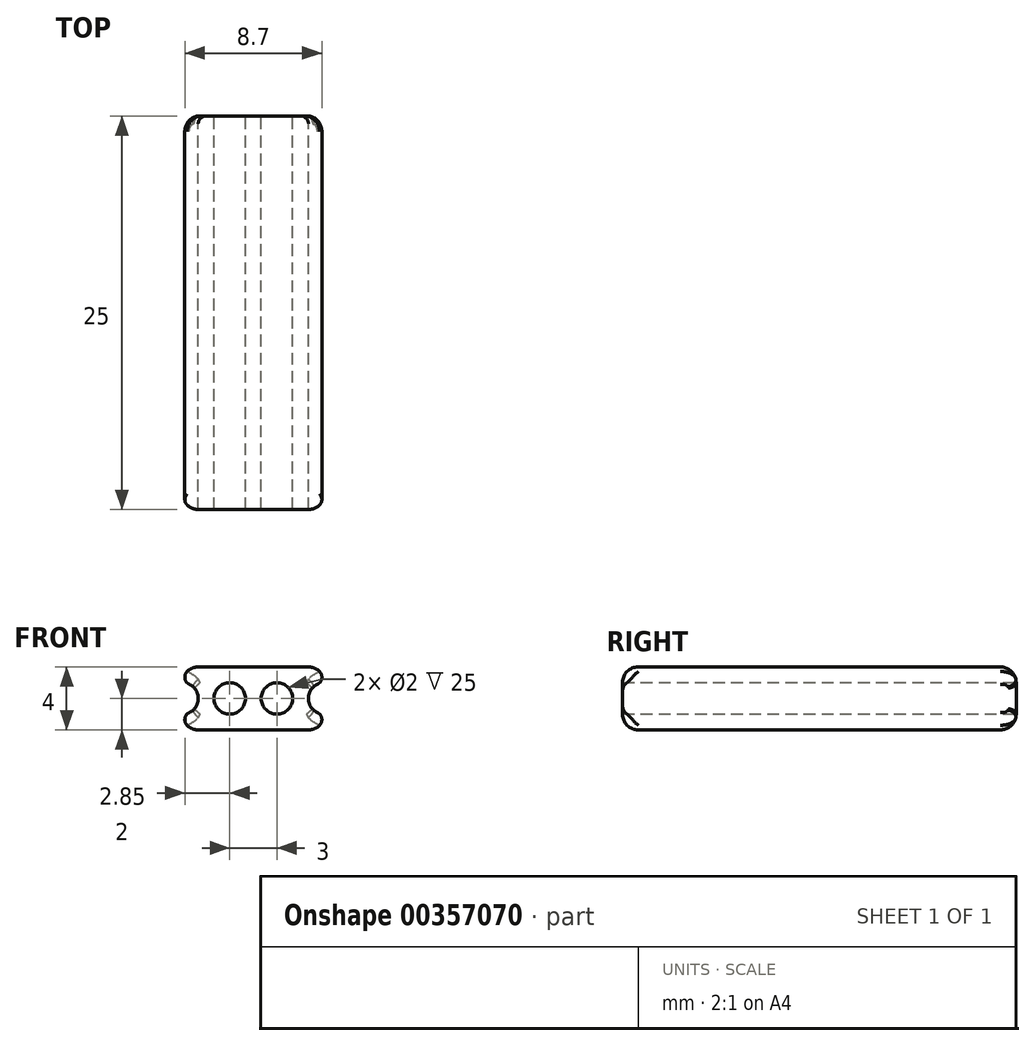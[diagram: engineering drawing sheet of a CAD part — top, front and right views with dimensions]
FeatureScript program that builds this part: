
annotation { "Feature Type Name" : "Feature", "Feature Type Description" : "" }
export const myFeature = defineFeature(function(context is Context, id is Id, definition is map)
    precondition{}
    {
        {
            var Q0;
            Q0=qCreatedBy(makeId("Front.planeOp"),FACE);
            var sketch = newSketch(context, id + "F0", { "sketchPlane" : qUnion([Q0])});
            skLineSegment(sketch, "E0.bottom", {"start": v(-4.5, 2) * mm, "end": v(4.5, 2) * mm});
            skLineSegment(sketch, "E0.top", {"start": v(-4.5, -2) * mm, "end": v(4.5, -2) * mm});
            skLineSegment(sketch, "E0.left", {"start": v(-4.5, 2) * mm, "end": v(-4.5, -2) * mm});
            skLineSegment(sketch, "E0.right", {"start": v(4.5, 2) * mm, "end": v(4.5, -2) * mm});
            skPoint(sketch, "E1", {"position": v(0, 2) * mm});
            skPoint(sketch, "E2", {"position": v(-4.5, 0) * mm});
            skCircle(sketch, "E3", {"center": v(-4.5, 0) * mm, "radius": 1 * mm});
            skCircle(sketch, "E4.1.0.0", {"center": v(-1.5, 0) * mm, "radius": 1 * mm});
            skCircle(sketch, "E4.2.0.0", {"center": v(1.5, 0) * mm, "radius": 1 * mm});
            skCircle(sketch, "E4.3.0.0", {"center": v(4.5, 0) * mm, "radius": 1 * mm});
            skLineSegment(sketch, "E4.direction1", {"start": v(-4.5, 0) * mm, "end": v(-1.5, 0) * mm, "construction": true});
            skSolve(sketch);
        }
        {
            var Q0;
            Q0=makeQuery(id+"F0.imprint","IMPRINT",FACE,{"disambiguationData":[TD([[makeQuery(id+"F0.imprint","IMPRINT",EDGE,{"derivedFrom":sQuery(id+"F0.wireOp",EDGE,"E0.bottom")}),-1.0]])]});
            extrude(context, id + "F1", {"entities" : qUnion([Q0]), "endBound" : BoundingType.SYMMETRIC, "depth" : 25 * mm, "offsetDistance" : 25 * mm});
        }
        {
            var Q0;
            Q0=makeQuery(id+"F1.opExtrude","SWEPT_FACE",FACE,{"disambiguationData":[OSD([sQuery(id+"F0.wireOp",EDGE,"E0.bottom")])]});
            var Q1;
            Q1=makeQuery(id+"F1.opExtrude","SWEPT_FACE",FACE,{"disambiguationData":[OSD([sQuery(id+"F0.wireOp",EDGE,"E0.top")])]});
            var Q2;
            {var subQ0=sQuery(id+"F0.wireOp",EDGE,"E0.right");Q2=makeQuery(id+"F1.opExtrude","CAP_EDGE",EDGE,{"disambiguationData":[OSD([subQ0]),TDD([makeQuery(id+"F0.imprint","IMPRINT",EDGE,{"disambiguationData":[TD([[makeQuery(id+"F0.imprint","INTERSECT",VERTEX,{"derivedFrom":[sQuery(id+"F0.wireOp",EDGE,"E0.bottom"),subQ0]}),-1.0]])],"derivedFrom":subQ0})])],"isStart":false});}
            var Q3;
            {var subQ0=sQuery(id+"F0.wireOp",EDGE,"E0.right");Q3=makeQuery(id+"F1.opExtrude","CAP_EDGE",EDGE,{"disambiguationData":[OSD([subQ0]),TDD([makeQuery(id+"F0.imprint","IMPRINT",EDGE,{"disambiguationData":[TD([[makeQuery(id+"F0.imprint","INTERSECT",VERTEX,{"derivedFrom":[sQuery(id+"F0.wireOp",EDGE,"E0.top"),subQ0]}),1.0]])],"derivedFrom":subQ0})])],"isStart":false});}
            var Q4;
            {var subQ0=sQuery(id+"F0.wireOp",EDGE,"E0.left");Q4=makeQuery(id+"F1.opExtrude","CAP_EDGE",EDGE,{"disambiguationData":[OSD([subQ0]),TDD([makeQuery(id+"F0.imprint","IMPRINT",EDGE,{"disambiguationData":[TD([[makeQuery(id+"F0.imprint","INTERSECT",VERTEX,{"derivedFrom":[sQuery(id+"F0.wireOp",EDGE,"E0.bottom"),subQ0]}),-1.0]])],"derivedFrom":subQ0})])],"isStart":false});}
            var Q5;
            {var subQ0=sQuery(id+"F0.wireOp",EDGE,"E0.left");Q5=makeQuery(id+"F1.opExtrude","CAP_EDGE",EDGE,{"disambiguationData":[OSD([subQ0]),TDD([makeQuery(id+"F0.imprint","IMPRINT",EDGE,{"disambiguationData":[TD([[makeQuery(id+"F0.imprint","INTERSECT",VERTEX,{"derivedFrom":[sQuery(id+"F0.wireOp",EDGE,"E0.top"),subQ0]}),1.0]])],"derivedFrom":subQ0})])],"isStart":false});}
            var Q6;
            {var subQ0=sQuery(id+"F0.wireOp",EDGE,"E0.left");Q6=makeQuery(id+"F1.opExtrude","CAP_EDGE",EDGE,{"disambiguationData":[OSD([subQ0]),TDD([makeQuery(id+"F0.imprint","IMPRINT",EDGE,{"disambiguationData":[TD([[makeQuery(id+"F0.imprint","INTERSECT",VERTEX,{"derivedFrom":[sQuery(id+"F0.wireOp",EDGE,"E0.bottom"),subQ0]}),-1.0]])],"derivedFrom":subQ0})])],"isStart":true});}
            var Q7;
            {var subQ0=sQuery(id+"F0.wireOp",EDGE,"E0.left");Q7=makeQuery(id+"F1.opExtrude","CAP_EDGE",EDGE,{"disambiguationData":[OSD([subQ0]),TDD([makeQuery(id+"F0.imprint","IMPRINT",EDGE,{"disambiguationData":[TD([[makeQuery(id+"F0.imprint","INTERSECT",VERTEX,{"derivedFrom":[sQuery(id+"F0.wireOp",EDGE,"E0.top"),subQ0]}),1.0]])],"derivedFrom":subQ0})])],"isStart":true});}
            var Q8;
            {var subQ0=sQuery(id+"F0.wireOp",EDGE,"E0.right");Q8=makeQuery(id+"F1.opExtrude","CAP_EDGE",EDGE,{"disambiguationData":[OSD([subQ0]),TDD([makeQuery(id+"F0.imprint","IMPRINT",EDGE,{"disambiguationData":[TD([[makeQuery(id+"F0.imprint","INTERSECT",VERTEX,{"derivedFrom":[sQuery(id+"F0.wireOp",EDGE,"E0.bottom"),subQ0]}),-1.0]])],"derivedFrom":subQ0})])],"isStart":true});}
            var Q9;
            {var subQ0=sQuery(id+"F0.wireOp",EDGE,"E0.right");Q9=makeQuery(id+"F1.opExtrude","CAP_EDGE",EDGE,{"disambiguationData":[OSD([subQ0]),TDD([makeQuery(id+"F0.imprint","IMPRINT",EDGE,{"disambiguationData":[TD([[makeQuery(id+"F0.imprint","INTERSECT",VERTEX,{"derivedFrom":[sQuery(id+"F0.wireOp",EDGE,"E0.top"),subQ0]}),1.0]])],"derivedFrom":subQ0})])],"isStart":true});}
            fillet(context, id + "F2", {"entities" : qUnion([Q0, Q1, Q2, Q3, Q4, Q5, Q6, Q7, Q8, Q9]), "radius" : 1 * mm, "tangentPropagation" : true, "allowEdgeOverflow" : false});
        }
        {
            var Q0;
            {var subQ0=sQuery(id+"F0.wireOp",EDGE,"E3");var subQ1=sQuery(id+"F0.wireOp",EDGE,"E0.left");Q0=makeQuery(id+"F2.opFillet","BLEND_EDGE",EDGE,{"blendedFrom":[makeQuery(id+"F1.opExtrude","CAP_EDGE",EDGE,{"disambiguationData":[OSD([subQ1]),TDD([makeQuery(id+"F0.imprint","IMPRINT",EDGE,{"disambiguationData":[TD([[makeQuery(id+"F0.imprint","INTERSECT",VERTEX,{"derivedFrom":[sQuery(id+"F0.wireOp",EDGE,"E0.bottom"),subQ1]}),-1.0]])],"derivedFrom":subQ1})])],"isStart":true}),makeQuery(id+"F1.opExtrude","SWEPT_FACE",FACE,{"disambiguationData":[OSD([subQ0])]})],"blendedInto":[makeQuery(id+"F1.opExtrude","SWEPT_FACE",FACE,{"disambiguationData":[OSD([subQ0])]})]});}
            var Q1;
            {var subQ0=sQuery(id+"F0.wireOp",EDGE,"E3");var subQ1=sQuery(id+"F0.wireOp",EDGE,"E0.left");Q1=makeQuery(id+"F2.opFillet","BLEND_EDGE",EDGE,{"blendedFrom":[makeQuery(id+"F1.opExtrude","CAP_EDGE",EDGE,{"disambiguationData":[OSD([subQ1]),TDD([makeQuery(id+"F0.imprint","IMPRINT",EDGE,{"disambiguationData":[TD([[makeQuery(id+"F0.imprint","INTERSECT",VERTEX,{"derivedFrom":[sQuery(id+"F0.wireOp",EDGE,"E0.top"),subQ1]}),1.0]])],"derivedFrom":subQ1})])],"isStart":true}),makeQuery(id+"F1.opExtrude","SWEPT_FACE",FACE,{"disambiguationData":[OSD([subQ0])]})],"blendedInto":[makeQuery(id+"F1.opExtrude","SWEPT_FACE",FACE,{"disambiguationData":[OSD([subQ0])]})]});}
            var Q2;
            {var subQ0=sQuery(id+"F0.wireOp",EDGE,"E4.3.0.0");var subQ1=sQuery(id+"F0.wireOp",EDGE,"E0.right");Q2=makeQuery(id+"F2.opFillet","BLEND_EDGE",EDGE,{"blendedFrom":[makeQuery(id+"F1.opExtrude","CAP_EDGE",EDGE,{"disambiguationData":[OSD([subQ1]),TDD([makeQuery(id+"F0.imprint","IMPRINT",EDGE,{"disambiguationData":[TD([[makeQuery(id+"F0.imprint","INTERSECT",VERTEX,{"derivedFrom":[sQuery(id+"F0.wireOp",EDGE,"E0.bottom"),subQ1]}),-1.0]])],"derivedFrom":subQ1})])],"isStart":true}),makeQuery(id+"F1.opExtrude","SWEPT_FACE",FACE,{"disambiguationData":[OSD([subQ0])]})],"blendedInto":[makeQuery(id+"F1.opExtrude","SWEPT_FACE",FACE,{"disambiguationData":[OSD([subQ0])]})]});}
            var Q3;
            {var subQ0=sQuery(id+"F0.wireOp",EDGE,"E4.3.0.0");var subQ1=sQuery(id+"F0.wireOp",EDGE,"E0.right");Q3=makeQuery(id+"F2.opFillet","BLEND_EDGE",EDGE,{"blendedFrom":[makeQuery(id+"F1.opExtrude","CAP_EDGE",EDGE,{"disambiguationData":[OSD([subQ1]),TDD([makeQuery(id+"F0.imprint","IMPRINT",EDGE,{"disambiguationData":[TD([[makeQuery(id+"F0.imprint","INTERSECT",VERTEX,{"derivedFrom":[sQuery(id+"F0.wireOp",EDGE,"E0.top"),subQ1]}),1.0]])],"derivedFrom":subQ1})])],"isStart":true}),makeQuery(id+"F1.opExtrude","SWEPT_FACE",FACE,{"disambiguationData":[OSD([subQ0])]})],"blendedInto":[makeQuery(id+"F1.opExtrude","SWEPT_FACE",FACE,{"disambiguationData":[OSD([subQ0])]})]});}
            fillet(context, id + "F3", {"entities" : qUnion([Q0, Q1, Q2, Q3]), "radius" : 0.5 * mm, "tangentPropagation" : true, "allowEdgeOverflow" : false});
        }
    });
